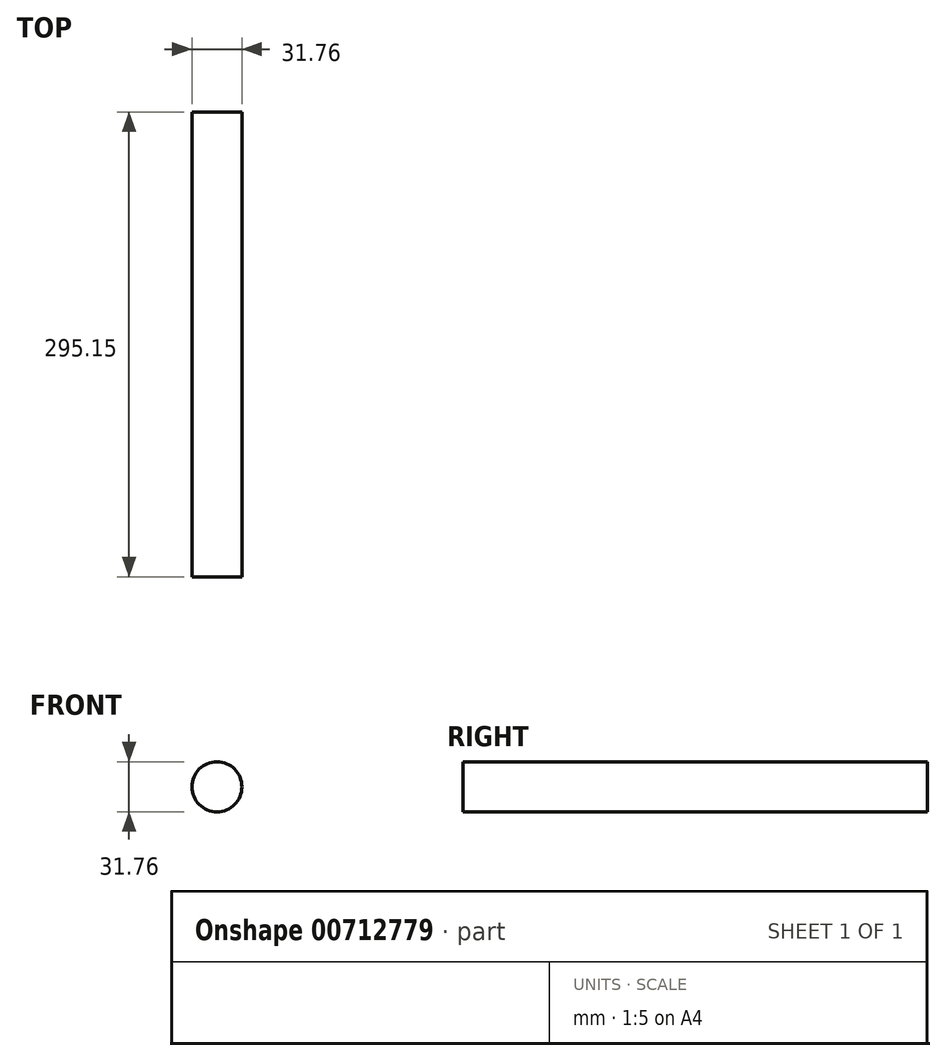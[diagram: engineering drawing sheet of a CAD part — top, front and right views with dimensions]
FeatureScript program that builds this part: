
annotation { "Feature Type Name" : "Feature", "Feature Type Description" : "" }
export const myFeature = defineFeature(function(context is Context, id is Id, definition is map)
    precondition{}
    {
        {
            var Q0;
            Q0=qCreatedBy(makeId("Front.planeOp"),FACE);
            var sketch = newSketch(context, id + "F0", { "sketchPlane" : qUnion([Q0])});
            skCircle(sketch, "E0", {"center": v(0, 0) * mm, "radius": 15.88 * mm});
            skSolve(sketch);
        }
        {
            var Q0;
            Q0 = qSketchRegion(id + "F0", true);
            extrude(context, id + "F1", {"entities" : qUnion([Q0]), "depth" : 295.15 * mm, "offsetDistance" : 25.4 * mm});
        }
    });
